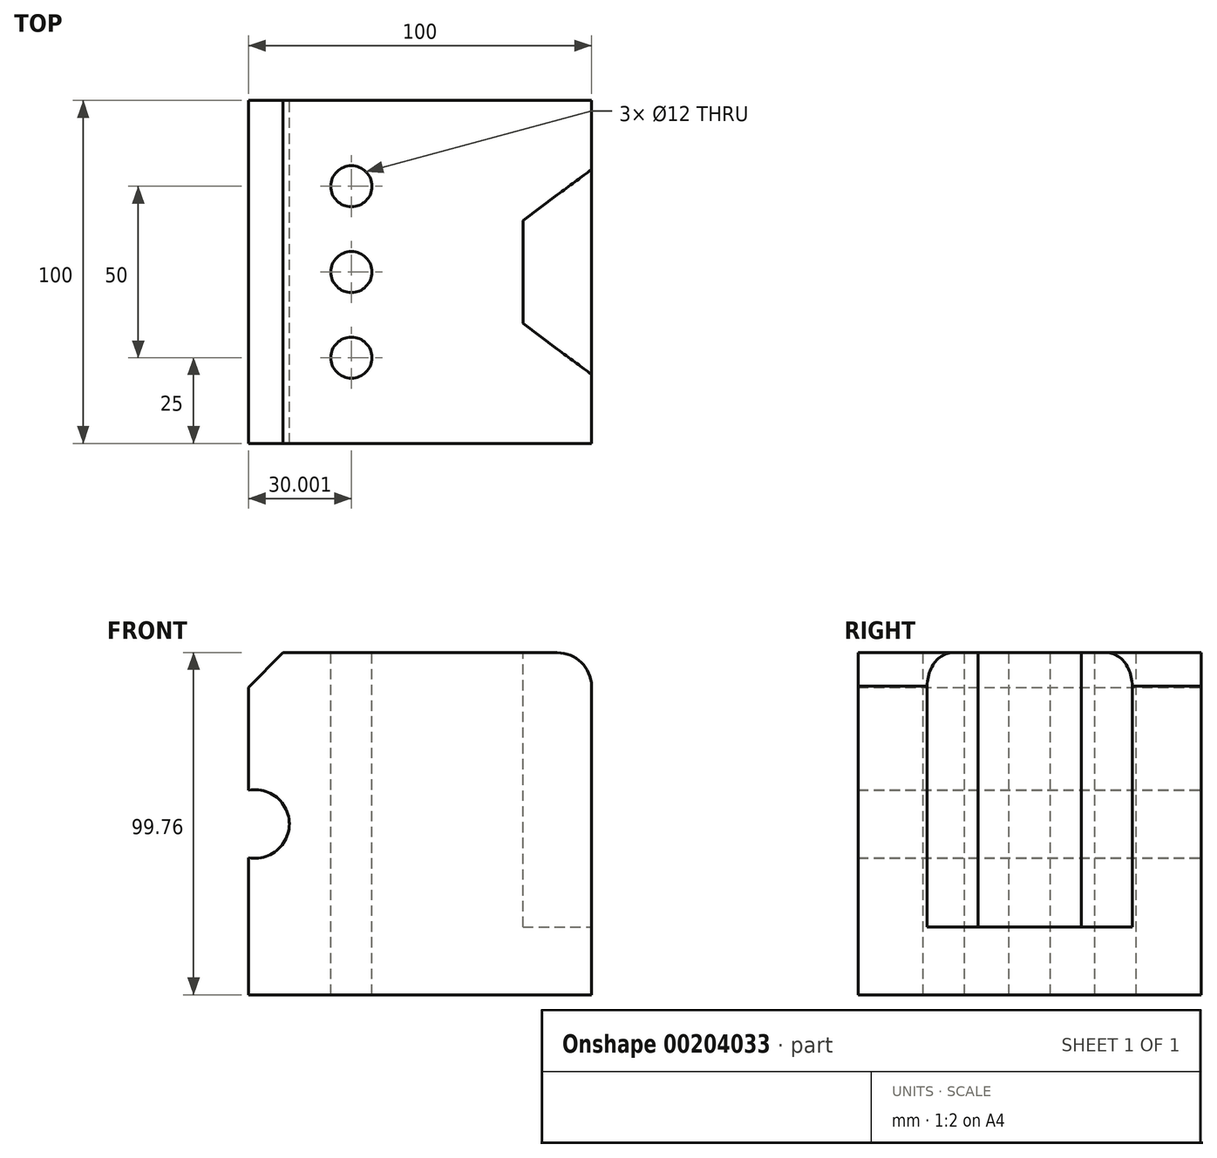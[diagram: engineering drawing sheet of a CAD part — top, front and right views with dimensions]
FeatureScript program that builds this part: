
annotation { "Feature Type Name" : "Feature", "Feature Type Description" : "" }
export const myFeature = defineFeature(function(context is Context, id is Id, definition is map)
    precondition{}
    {
        {
            var Q0;
            Q0=qCreatedBy(makeId("Front.planeOp"),FACE);
            var sketch = newSketch(context, id + "F0", { "sketchPlane" : qUnion([Q0])});
            skLineSegment(sketch, "E0", {"start": v(-41.94, 58) * mm, "end": v(38.06, 58) * mm});
            skArc(sketch, "E1", {"start": v(48.06, 48.24) * mm, "mid": v(45.05, 55.15) * mm, "end": v(38.06, 58) * mm});
            skLineSegment(sketch, "E2", {"start": v(48.06, 48.24) * mm, "end": v(48.06, -41.76) * mm});
            skLineSegment(sketch, "E3", {"start": v(48.06, -41.76) * mm, "end": v(-51.94, -41.76) * mm});
            skLineSegment(sketch, "E4", {"start": v(-51.94, -41.76) * mm, "end": v(-51.94, -1.76) * mm});
            skArc(sketch, "E5", {"start": v(-51.94, -1.76) * mm, "mid": v(-40.02, 8.06) * mm, "end": v(-51.94, 17.87) * mm});
            skLineSegment(sketch, "E6", {"start": v(-51.94, 17.87) * mm, "end": v(-51.94, 47.87) * mm});
            skLineSegment(sketch, "E7", {"start": v(-51.94, 47.87) * mm, "end": v(-41.94, 58) * mm});
            skSolve(sketch);
        }
        {
            var Q0;
            Q0 = qSketchRegion(id + "F0", true);
            extrude(context, id + "F1", {"entities" : qUnion([Q0]), "depth" : 100 * mm});
        }
        {
            var Q0;
            Q0=makeQuery(id+"F1.opExtrude","SWEPT_FACE",FACE,{"disambiguationData":[OSD([sQuery(id+"F0.wireOp",EDGE,"E0")])]});
            var sketch = newSketch(context, id + "F2", { "sketchPlane" : qUnion([Q0])});
            skCircle(sketch, "E8", {"center": v(-21.94, -25) * mm, "radius": 6 * mm});
            skCircle(sketch, "E9", {"center": v(-21.94, -75) * mm, "radius": 6 * mm});
            skCircle(sketch, "E10", {"center": v(-21.94, -50) * mm, "radius": 6 * mm});
            skSolve(sketch);
        }
        {
            var Q0;
            Q0 = qSketchRegion(id + "F2", true);
            var Q1;
            Q1=sQuery(id+"F2.wireOp",EDGE,"E8");
            extrude(context, id + "F3", {"entities" : qUnion([Q0]), "operationType" : NewBodyOperationType.REMOVE, "surfaceEntities" : qUnion([Q1]), "oppositeDirection" : true, "depth" : 100 * mm});
        }
        {
            var Q0;
            Q0=makeQuery(id+"F1.opExtrude","SWEPT_FACE",FACE,{"disambiguationData":[OSD([sQuery(id+"F0.wireOp",EDGE,"E0")])]});
            var sketch = newSketch(context, id + "F4", { "sketchPlane" : qUnion([Q0])});
            skSolve(sketch);
        }
        {
            var Q0;
            {var subQ0=sQuery(id+"F0.wireOp",EDGE,"E0");Q0=makeQuery(id+"F4.imprint","IMPRINT",FACE,{"disambiguationData":[TD([[makeQuery(id+"F4.imprint","IMPRINT",EDGE,{"derivedFrom":makeQuery(id+"F1.opExtrude","CAP_EDGE",EDGE,{"disambiguationData":[OSD([subQ0])],"isStart":true})}),-1.0]])]});}
            var sketch = newSketch(context, id + "F5", { "sketchPlane" : qUnion([Q0])});
            skLineSegment(sketch, "E11", {"start": v(28.06, -35) * mm, "end": v(28.06, -65) * mm});
            skLineSegment(sketch, "E12", {"start": v(28.06, -35) * mm, "end": v(48.2, -20) * mm});
            skLineSegment(sketch, "E13", {"start": v(28.06, -65) * mm, "end": v(48.2, -80) * mm});
            skLineSegment(sketch, "E14", {"start": v(48.2, -20) * mm, "end": v(48.2, -80) * mm});
            skSolve(sketch);
        }
        {
            var Q0;
            Q0 = qSketchRegion(id + "F5", true);
            extrude(context, id + "F6", {"entities" : qUnion([Q0]), "operationType" : NewBodyOperationType.REMOVE, "oppositeDirection" : true, "depth" : 80 * mm});
        }
    });
